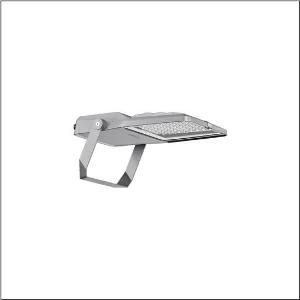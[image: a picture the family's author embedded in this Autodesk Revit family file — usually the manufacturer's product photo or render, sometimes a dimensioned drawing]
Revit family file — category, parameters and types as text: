
# Revit family: floodlight_fl_21_iq_mini___pl61_5xa7772c2c1a_b30e
name_source: partatom
category: Lighting Fixtures
units: mm (PartAtom-declared; Revit-internal decimal feet)

## family parameters
Cut with Voids When Loaded = No
Host = Face
Light Source = No
Part Type = Normal
Room Calculation Point = No
Round Connector Dimension = Use Diameter
Shared = No

## types (1)
- --- (1 x LED, 11980 lm, 87.2 W, 3000K)
    Apparent Load = 87 VA
    CIE Flux Codes = 33 65 98 100 100
    Color Rendering = 70
    Color Temperature = 3000K
    Default Elevation = 1800 mm
    Description = Floodlight FL 21 iQ mini, floodlight, primary light control with lens, of PMMA, primary optical cover: protective disc, of toughened safety glass, transparent, light distribution: PL61, light emission: direct distribution, installation type: surface-mounted, LED, High Power LED, rated luminous flux: 11.980lm, luminous efficacy: 137lm/W, light colour: 730, colour temperature: 3000K, control: Street-Remote, Auto-Match, Temp-Guard, Night-Set, Smart-Wire, Desk-Remote (wireless, voltage-free reading and setting of iQ features in the workshop via application-optimized NFC function/RFID function), optimised constant luminous flux control (CLO 2.0), with terminal, 6-pole, mains connection: 220..240V, AC, 50/60Hz, start of lifetime: 87W, end of service life: 92W, reduction: 40W, luminaire housing, of diecast aluminium, powder-coated, Siteco® metallic grey (DB 702S), corrosivity category C5 mid according to DIN EN ISO 12944, sealing non-destructively replaceable, mounting bracket, of steel, galvanised, powder-coated, Siteco® metallic grey (DB 702S), protection rating (complete): IP66, insulation class (complete): insulation class II (safety insulation), certification: CE, ENEC, VDE, protection symbol: D, impact resistance: IK08, permissible operating ambient temperature: -40..+40°C, permissible operating ambient temperature for outdoor applications: -40..+50°C, standard: DIN EN 12944, LABS conformity tested according to VDMA 24364:2018-05, packaging unit: 1 piece

Light Distribution: PL61
    Height = 70 mm
    Lamp = 1 x LED
    Lamp Light Flux = 11980 lm
    Lamp Power = 87.2 W
    Lamp count = 1
    Length = 485 mm
    Luminous efficacy = 137 lm/W
    Manufacturer = Siteco
    ModVariant = No
    Model = 5XA7772C2C1A
    Number of Poles = 1
    OnlyDefault = Yes
    Power Factor = 1
    Product Name = Floodlight FL 21 iQ mini | PL61
    Product group = floodlight | pylon annexe
    ProductGroupID = 6200
    Protection Class = Protection class II
    Protection Degree = IP 66
    RLX_Detail_Level = 1
    RLX_Emergency_Light_Flux = 0 lm
    RLX_Emergency_Type = 0
    RLX_Emergency_Type_DB = No
    RlxData = <blob elided: 96421 chars, md5=a4637faa>
    Socket = socket
    Standby Power = 0 W
    System Light Flux = 11980 lm
    System Power = 87 W
    Type Comments = factory setting: luminous flux: 100 % | dim-lin: 254 | 456 mA
    Type Image = l_1006845.jpg
    URL = http://relux.com
    VarID = @adj_106191
    Voltage = 0 V
    Weight = 0.00 kg
    Width = 337 mm

## geometry (parser evidence)
native form markers: Blend x4, Sweep x10
no freeform markers — native parametric forms only
